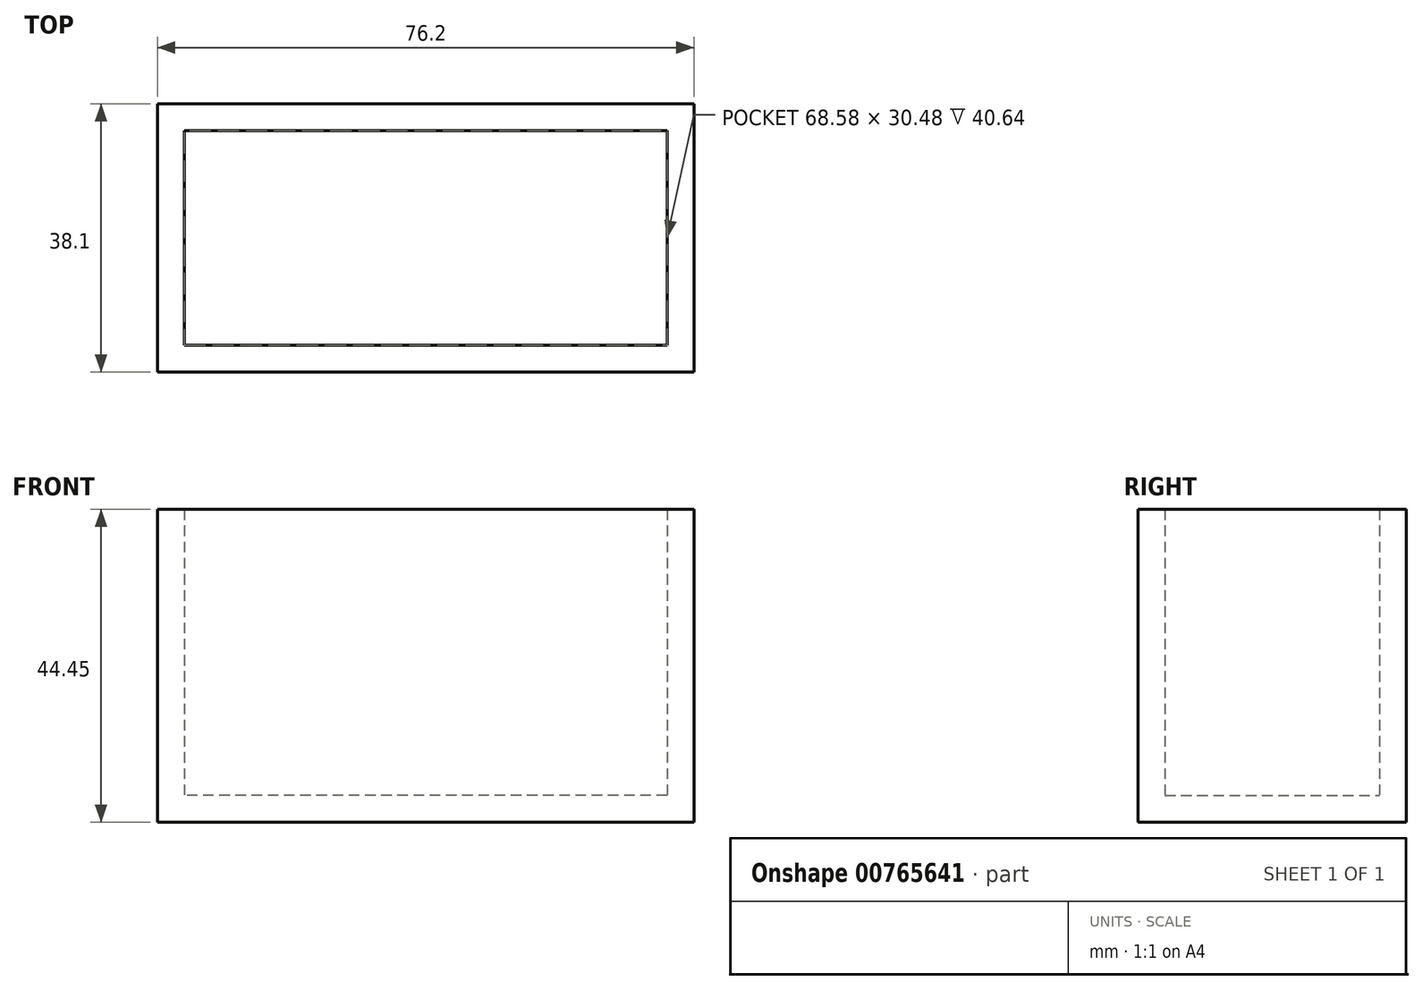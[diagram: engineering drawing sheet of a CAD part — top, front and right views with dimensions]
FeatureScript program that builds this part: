
annotation { "Feature Type Name" : "Feature", "Feature Type Description" : "" }
export const myFeature = defineFeature(function(context is Context, id is Id, definition is map)
    precondition{}
    {
        {
            var Q0;
            Q0=qCreatedBy(makeId("Top.planeOp"),FACE);
            var sketch = newSketch(context, id + "F0", { "sketchPlane" : qUnion([Q0])});
            skLineSegment(sketch, "E0.bottom", {"start": v(38.1, -19.05) * mm, "end": v(-38.1, -19.05) * mm});
            skLineSegment(sketch, "E0.top", {"start": v(38.1, 19.05) * mm, "end": v(-38.1, 19.05) * mm});
            skLineSegment(sketch, "E0.left", {"start": v(38.1, -19.05) * mm, "end": v(38.1, 19.05) * mm});
            skLineSegment(sketch, "E0.right", {"start": v(-38.1, -19.05) * mm, "end": v(-38.1, 19.05) * mm});
            skPoint(sketch, "E0.middle", {"position": v(0, 0) * mm});
            skSolve(sketch);
        }
        {
            var Q0;
            Q0=makeQuery(id+"F0.imprint","IMPRINT",FACE,{"disambiguationData":[TD([[makeQuery(id+"F0.imprint","IMPRINT",EDGE,{"derivedFrom":sQuery(id+"F0.wireOp",EDGE,"E0.bottom")}),-1.0]])]});
            extrude(context, id + "F1", {"entities" : qUnion([Q0]), "depth" : 44.45 * mm, "offsetDistance" : 25.4 * mm});
        }
        {
            var Q0;
            Q0=makeQuery(id+"F1.opExtrude","CAP_FACE",FACE,{"disambiguationData":[OSD([sQuery(id+"F0.wireOp",EDGE,"E0.bottom"),sQuery(id+"F0.wireOp",EDGE,"E0.top"),sQuery(id+"F0.wireOp",EDGE,"E0.left"),sQuery(id+"F0.wireOp",EDGE,"E0.right")])],"isStart":false});
            shell(context, id + "F2", {"entities" : qUnion([Q0]), "thickness" : 3.8 * mm});
        }
        {
            var Q0;
            Q0=makeQuery(id+"F1.opExtrude","SWEPT_FACE",FACE,{"disambiguationData":[OSD([sQuery(id+"F0.wireOp",EDGE,"E0.left")])]});
            var sketch = newSketch(context, id + "F3", { "sketchPlane" : qUnion([Q0])});
            skLineSegment(sketch, "E1.0", {"start": v(-19.05, 44.45) * mm, "end": v(-19.05, 0) * mm});
            skLineSegment(sketch, "E2.0", {"start": v(19.05, 44.45) * mm, "end": v(19.05, 0) * mm});
            skSolve(sketch);
        }
    });
